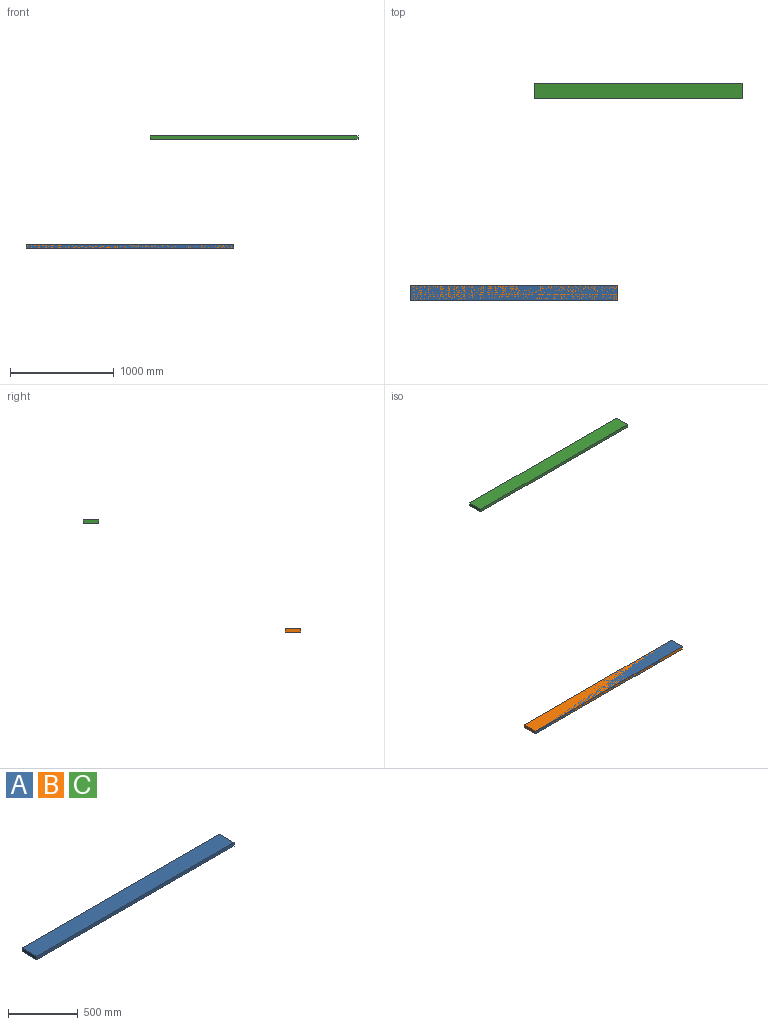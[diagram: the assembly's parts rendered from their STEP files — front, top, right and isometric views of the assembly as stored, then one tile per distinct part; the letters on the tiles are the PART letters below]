
ASSEMBLY  parts=3 mates=1
PART A: 6 faces, bbox 2000x150x30 mm
  f0: plane 150x30mm, normal (1,0,0), area 4500mm2, adj f1,f3,f4,f5
  f1: plane 2000x30mm, normal (0,1,0), area 60000mm2, adj f0,f2,f4,f5
  f2: plane 150x30mm, normal (-1,0,0), area 4500mm2, adj f1,f3,f4,f5
  f3: plane 2000x30mm, normal (0,-1,0), area 60000mm2, adj f0,f2,f4,f5
  f4: plane 2000x150mm, normal (0,0,1), area 300000mm2, adj f0,f1,f2,f3
  f5: plane 2000x150mm, normal (0,0,-1), area 300000mm2, adj f0,f1,f2,f3
PART B: same geometry as A
PART C: same geometry as A
PLACE A rot(axis=(0,1,0),0deg) t=(141.23,-542.66,-457.7)mm
PLACE B t=(141.23,-542.66,-457.7)mm
PLACE C t=(1337.84,1398.46,591.3)mm
MATE pin_slot A.f3 <-> B.f3  axis (0,-1,0) through (141.23,-617.66,-442.7)mm
